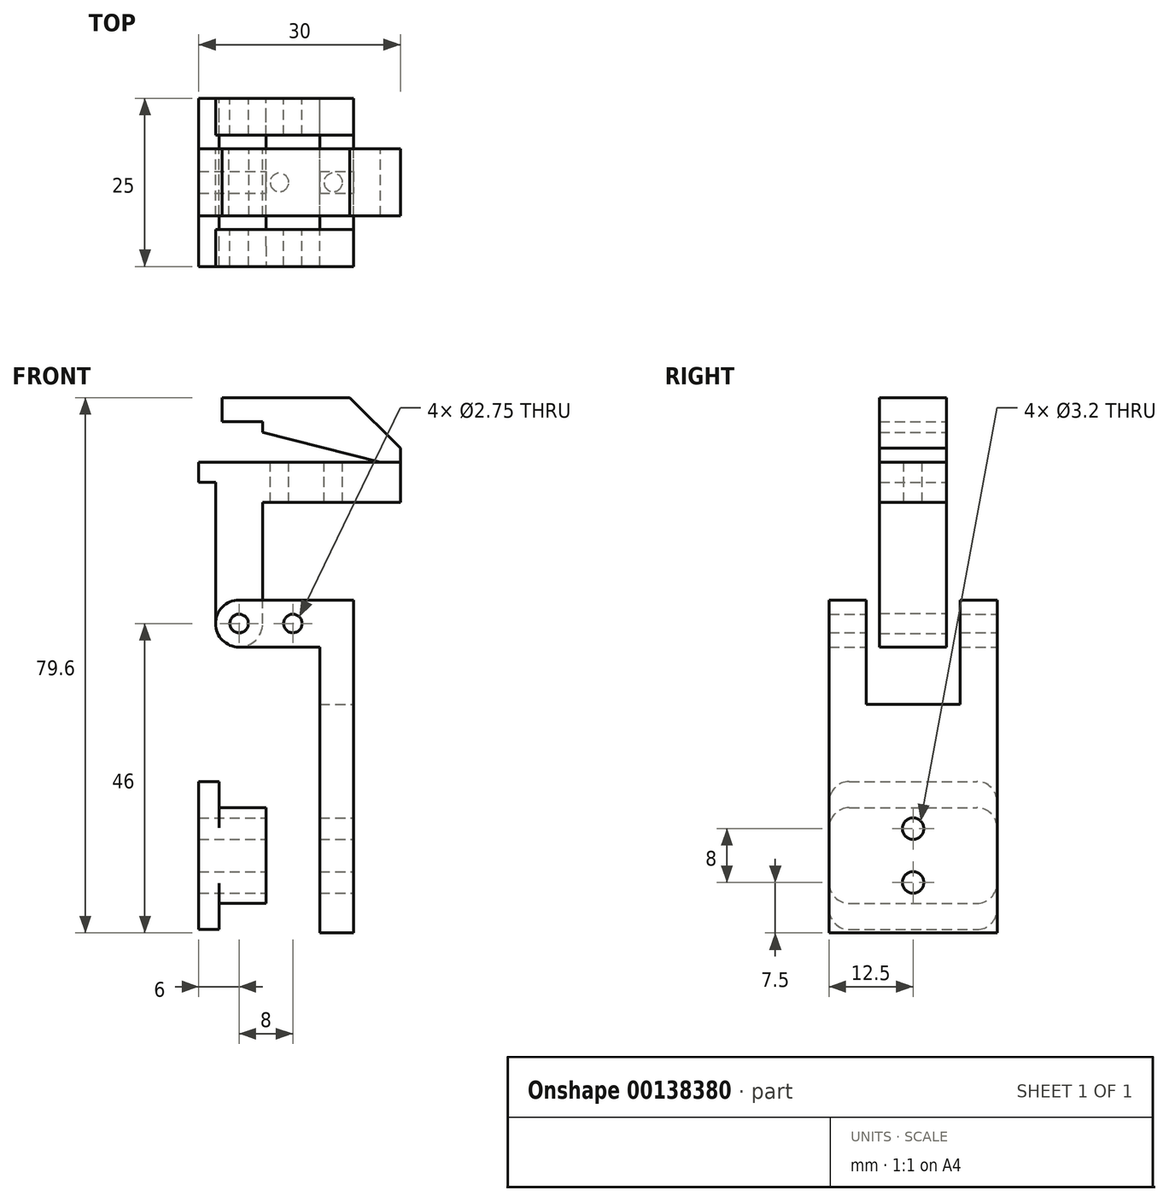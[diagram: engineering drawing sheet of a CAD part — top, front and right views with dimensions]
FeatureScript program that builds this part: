
annotation { "Feature Type Name" : "Feature", "Feature Type Description" : "" }
export const myFeature = defineFeature(function(context is Context, id is Id, definition is map)
    precondition{}
    {
        {
            var Q0;
            Q0=qCreatedBy(makeId("Front.planeOp"),FACE);
            var sketch = newSketch(context, id + "F0", { "sketchPlane" : qUnion([Q0])});
            skLineSegment(sketch, "E0.bottom", {"start": v(7.5, -7.5) * mm, "end": v(-7.5, -7.5) * mm, "construction": true});
            skLineSegment(sketch, "E0.top", {"start": v(7.5, 7.5) * mm, "end": v(-7.5, 7.5) * mm, "construction": true});
            skLineSegment(sketch, "E0.left", {"start": v(7.5, -7.5) * mm, "end": v(7.5, 7.5) * mm, "construction": true});
            skLineSegment(sketch, "E0.right", {"start": v(-7.5, -7.5) * mm, "end": v(-7.5, 7.5) * mm, "construction": true});
            skPoint(sketch, "E0.middle", {"position": v(0, 0) * mm});
            skLineSegment(sketch, "E1.bottom", {"start": v(7.5, -37.5) * mm, "end": v(-7.5, -37.5) * mm, "construction": true});
            skLineSegment(sketch, "E1.top", {"start": v(7.5, -22.5) * mm, "end": v(-7.5, -22.5) * mm, "construction": true});
            skLineSegment(sketch, "E1.left", {"start": v(7.5, -37.5) * mm, "end": v(7.5, -22.5) * mm, "construction": true});
            skLineSegment(sketch, "E1.right", {"start": v(-7.5, -37.5) * mm, "end": v(-7.5, -22.5) * mm, "construction": true});
            skPoint(sketch, "E1.middle", {"position": v(0, -30) * mm});
            skLineSegment(sketch, "E2", {"start": v(0, -7.5) * mm, "end": v(0, -22.5) * mm, "construction": true});
            skSolve(sketch);
        }
        {
            var Q0;
            Q0=qCreatedBy(makeId("Front.planeOp"),FACE);
            var sketch = newSketch(context, id + "F1", { "sketchPlane" : qUnion([Q0])});
            skLineSegment(sketch, "E3.bottom", {"start": v(-10.5, -4) * mm, "end": v(-7.5, -4) * mm});
            skLineSegment(sketch, "E3.top", {"start": v(-10.5, -26) * mm, "end": v(-7.5, -26) * mm});
            skLineSegment(sketch, "E3.left", {"start": v(-10.5, -4) * mm, "end": v(-10.5, -26) * mm});
            skLineSegment(sketch, "E3.right", {"start": v(-7.5, -4) * mm, "end": v(-7.5, -7.9) * mm});
            skLineSegment(sketch, "E4.bottom", {"start": v(-7.5, -7.9) * mm, "end": v(-0.5, -7.9) * mm});
            skLineSegment(sketch, "E4.top", {"start": v(-7.5, -22.1) * mm, "end": v(-0.5, -22.1) * mm});
            skLineSegment(sketch, "E4.right", {"start": v(-0.5, -7.9) * mm, "end": v(-0.5, -22.1) * mm});
            skLineSegment(sketch, "E5.trimOffspring", {"start": v(-7.5, -22.1) * mm, "end": v(-7.5, -26) * mm});
            skLineSegment(sketch, "E6", {"start": v(-0.5, -15) * mm, "end": v(0, -15) * mm, "construction": true});
            skPoint(sketch, "E7", {"position": v(-0.5, -11) * mm});
            skPoint(sketch, "E8", {"position": v(-0.5, -19) * mm});
            skSolve(sketch);
        }
        {
            var Q0;
            Q0 = qSketchRegion(id + "F1", true);
            extrude(context, id + "F2", {"entities" : qUnion([Q0]), "endBound" : BoundingType.SYMMETRIC, "depth" : 25 * mm});
        }
        {
            var Q0;
            Q0=makeQuery(id+"F2.opExtrude","CAP_EDGE",EDGE,{"disambiguationData":[OSD([sQuery(id+"F1.wireOp",EDGE,"E4.bottom")])],"isStart":false});
            var Q1;
            Q1=makeQuery(id+"F2.opExtrude","CAP_EDGE",EDGE,{"disambiguationData":[OSD([sQuery(id+"F1.wireOp",EDGE,"E3.bottom")])],"isStart":false});
            var Q2;
            Q2=makeQuery(id+"F2.opExtrude","CAP_EDGE",EDGE,{"disambiguationData":[OSD([sQuery(id+"F1.wireOp",EDGE,"E3.top")])],"isStart":false});
            var Q3;
            Q3=makeQuery(id+"F2.opExtrude","CAP_EDGE",EDGE,{"disambiguationData":[OSD([sQuery(id+"F1.wireOp",EDGE,"E4.top")])],"isStart":false});
            var Q4;
            Q4=makeQuery(id+"F2.opExtrude","CAP_EDGE",EDGE,{"disambiguationData":[OSD([sQuery(id+"F1.wireOp",EDGE,"E4.bottom")])],"isStart":true});
            var Q5;
            Q5=makeQuery(id+"F2.opExtrude","CAP_EDGE",EDGE,{"disambiguationData":[OSD([sQuery(id+"F1.wireOp",EDGE,"E3.bottom")])],"isStart":true});
            var Q6;
            Q6=makeQuery(id+"F2.opExtrude","CAP_EDGE",EDGE,{"disambiguationData":[OSD([sQuery(id+"F1.wireOp",EDGE,"E3.top")])],"isStart":true});
            var Q7;
            Q7=makeQuery(id+"F2.opExtrude","CAP_EDGE",EDGE,{"disambiguationData":[OSD([sQuery(id+"F1.wireOp",EDGE,"E4.top")])],"isStart":true});
            fillet(context, id + "F3", {"entities" : qUnion([Q0, Q1, Q2, Q3, Q4, Q5, Q6, Q7]), "radius" : 3 * mm, "tangentPropagation" : true, "allowEdgeOverflow" : false});
        }
        {
            var Q0;
            Q0=makeQuery(id+"F2.opExtrude","SWEPT_FACE",FACE,{"disambiguationData":[OSD([sQuery(id+"F1.wireOp",EDGE,"E4.right")])]});
            var sketch = newSketch(context, id + "F4", { "sketchPlane" : qUnion([Q0])});
            skCircle(sketch, "E9", {"center": v(0, -11) * mm, "radius": 1.38 * mm});
            skCircle(sketch, "E10", {"center": v(0, -19) * mm, "radius": 1.38 * mm});
            skSolve(sketch);
        }
        {
            var Q0;
            Q0 = qSketchRegion(id + "F4", true);
            extrude(context, id + "F5", {"entities" : qUnion([Q0]), "operationType" : NewBodyOperationType.REMOVE, "endBound" : BoundingType.THROUGH_ALL, "oppositeDirection" : true, "depth" : 25 * mm});
        }
        {
            var Q0;
            Q0=qCreatedBy(makeId("Front.planeOp"),FACE);
            var sketch = newSketch(context, id + "F6", { "sketchPlane" : qUnion([Q0])});
            skLineSegment(sketch, "E11", {"start": v(-4.5, 16) * mm, "end": v(7.5, 16) * mm});
            skLineSegment(sketch, "E12", {"start": v(7.5, 16) * mm, "end": v(7.5, -26.5) * mm});
            skLineSegment(sketch, "E13", {"start": v(7.5, -26.5) * mm, "end": v(12.5, -26.5) * mm});
            skLineSegment(sketch, "E14", {"start": v(12.5, -26.5) * mm, "end": v(12.5, 23) * mm});
            skLineSegment(sketch, "E15", {"start": v(12.5, 23) * mm, "end": v(-4.5, 23) * mm});
            skLineSegment(sketch, "E16", {"start": v(-4.5, 23) * mm, "end": v(-4.5, 16) * mm, "construction": true});
            skArc(sketch, "E17", {"start": v(-4.5, 23) * mm, "mid": v(-8, 19.5) * mm, "end": v(-4.5, 16) * mm});
            skCircle(sketch, "E18", {"center": v(-4.5, 19.5) * mm, "radius": 1.38 * mm});
            skLineSegment(sketch, "E19", {"start": v(-4.5, 19.5) * mm, "end": v(3.5, 19.5) * mm, "construction": true});
            skCircle(sketch, "E20", {"center": v(3.5, 19.5) * mm, "radius": 1.38 * mm});
            skSolve(sketch);
        }
        {
            var Q0;
            Q0=makeQuery(id+"F6.imprint","IMPRINT",FACE,{"disambiguationData":[TD([[makeQuery(id+"F6.imprint","IMPRINT",EDGE,{"derivedFrom":sQuery(id+"F6.wireOp",EDGE,"E11")}),1.0]])]});
            var Q1;
            Q1 = qSketchRegion(id + "F6", true);
            extrude(context, id + "F7", {"entities" : qUnion([Q0, Q1]), "endBound" : BoundingType.SYMMETRIC, "depth" : 25 * mm});
        }
        {
            var Q0;
            Q0=makeQuery(id+"F7.opExtrude","SWEPT_FACE",FACE,{"disambiguationData":[OSD([sQuery(id+"F6.wireOp",EDGE,"E14")])]});
            var sketch = newSketch(context, id + "F8", { "sketchPlane" : qUnion([Q0])});
            skLineSegment(sketch, "E21.bottom", {"start": v(-7, 23) * mm, "end": v(7, 23) * mm});
            skLineSegment(sketch, "E21.top", {"start": v(-7, 7.5) * mm, "end": v(7, 7.5) * mm});
            skLineSegment(sketch, "E21.left", {"start": v(-7, 23) * mm, "end": v(-7, 7.5) * mm});
            skLineSegment(sketch, "E21.right", {"start": v(7, 23) * mm, "end": v(7, 7.5) * mm});
            skPoint(sketch, "E22", {"position": v(0, 23) * mm});
            skCircle(sketch, "E23", {"center": v(0, -11) * mm, "radius": 1.6 * mm});
            skCircle(sketch, "E24", {"center": v(0, -19) * mm, "radius": 1.6 * mm});
            skSolve(sketch);
        }
        {
            var Q0;
            Q0 = qSketchRegion(id + "F8", true);
            extrude(context, id + "F9", {"entities" : qUnion([Q0]), "operationType" : NewBodyOperationType.REMOVE, "endBound" : BoundingType.THROUGH_ALL, "oppositeDirection" : true, "depth" : 25 * mm});
        }
        {
            var Q0;
            Q0=qCreatedBy(makeId("Front.planeOp"),FACE);
            var sketch = newSketch(context, id + "F10", { "sketchPlane" : qUnion([Q0])});
            skCircle(sketch, "E25", {"center": v(-4.5, 19.5) * mm, "radius": 1.5 * mm});
            skLineSegment(sketch, "E26.bottom", {"start": v(-8, 19.5) * mm, "end": v(-1, 19.5) * mm, "construction": true});
            skLineSegment(sketch, "E26.left", {"start": v(-8, 19.5) * mm, "end": v(-8, 40.5) * mm});
            skLineSegment(sketch, "E26.right", {"start": v(-1, 19.5) * mm, "end": v(-1, 37.5) * mm});
            skArc(sketch, "E27", {"start": v(-8, 19.5) * mm, "mid": v(-4.5, 16) * mm, "end": v(-1, 19.5) * mm});
            skLineSegment(sketch, "E28", {"start": v(-8, 40.5) * mm, "end": v(-10.5, 40.5) * mm});
            skLineSegment(sketch, "E29", {"start": v(-10.5, 40.5) * mm, "end": v(-10.5, 43.5) * mm});
            skLineSegment(sketch, "E30", {"start": v(-10.5, 43.5) * mm, "end": v(19.5, 43.5) * mm});
            skLineSegment(sketch, "E31", {"start": v(19.5, 43.5) * mm, "end": v(19.5, 37.5) * mm});
            skLineSegment(sketch, "E32", {"start": v(19.5, 37.5) * mm, "end": v(-1, 37.5) * mm});
            skCircle(sketch, "E33", {"center": v(-4.5, 19.5) * mm, "radius": 35 * mm, "construction": true});
            skPoint(sketch, "E34", {"position": v(1.5, 43.5) * mm});
            skPoint(sketch, "E35", {"position": v(9.5, 43.5) * mm});
            skSolve(sketch);
        }
        {
            var Q0;
            Q0 = qSketchRegion(id + "F10", true);
            extrude(context, id + "F11", {"entities" : qUnion([Q0]), "endBound" : BoundingType.SYMMETRIC, "depth" : 10 * mm});
        }
        {
            var Q0;
            Q0=makeQuery(id+"F11.opExtrude","SWEPT_FACE",FACE,{"disambiguationData":[OSD([sQuery(id+"F10.wireOp",EDGE,"E30")])]});
            var sketch = newSketch(context, id + "F12", { "sketchPlane" : qUnion([Q0])});
            skCircle(sketch, "E36", {"center": v(1.5, 0) * mm, "radius": 1.38 * mm});
            skCircle(sketch, "E37", {"center": v(9.5, 0) * mm, "radius": 1.38 * mm});
            skSolve(sketch);
        }
        {
            var Q0;
            Q0 = qSketchRegion(id + "F12", true);
            extrude(context, id + "F13", {"entities" : qUnion([Q0]), "operationType" : NewBodyOperationType.REMOVE, "oppositeDirection" : true, "depth" : 12 * mm});
        }
        {
            var Q0;
            Q0=qCreatedBy(makeId("Front.planeOp"),FACE);
            var sketch = newSketch(context, id + "F14", { "sketchPlane" : qUnion([Q0])});
            skLineSegment(sketch, "E38.bottom", {"start": v(-7, 53.1) * mm, "end": v(11.98, 53.1) * mm});
            skLineSegment(sketch, "E38.top", {"start": v(-7, 49.5) * mm, "end": v(-1, 49.5) * mm});
            skLineSegment(sketch, "E38.left", {"start": v(-7, 53.1) * mm, "end": v(-7, 49.5) * mm});
            skLineSegment(sketch, "E39", {"start": v(-1, 49.5) * mm, "end": v(-1, 47.9) * mm});
            skLineSegment(sketch, "E40", {"start": v(-1, 47.9) * mm, "end": v(16.5, 43.5) * mm});
            skLineSegment(sketch, "E41", {"start": v(16.5, 43.5) * mm, "end": v(19.5, 43.5) * mm});
            skLineSegment(sketch, "E42", {"start": v(19.5, 43.5) * mm, "end": v(19.5, 45.58) * mm});
            skLineSegment(sketch, "E43", {"start": v(19.5, 45.58) * mm, "end": v(11.98, 53.1) * mm});
            skSolve(sketch);
        }
        {
            var Q0;
            Q0 = qSketchRegion(id + "F14", true);
            extrude(context, id + "F15", {"entities" : qUnion([Q0]), "endBound" : BoundingType.SYMMETRIC, "depth" : 10 * mm});
        }
    });
